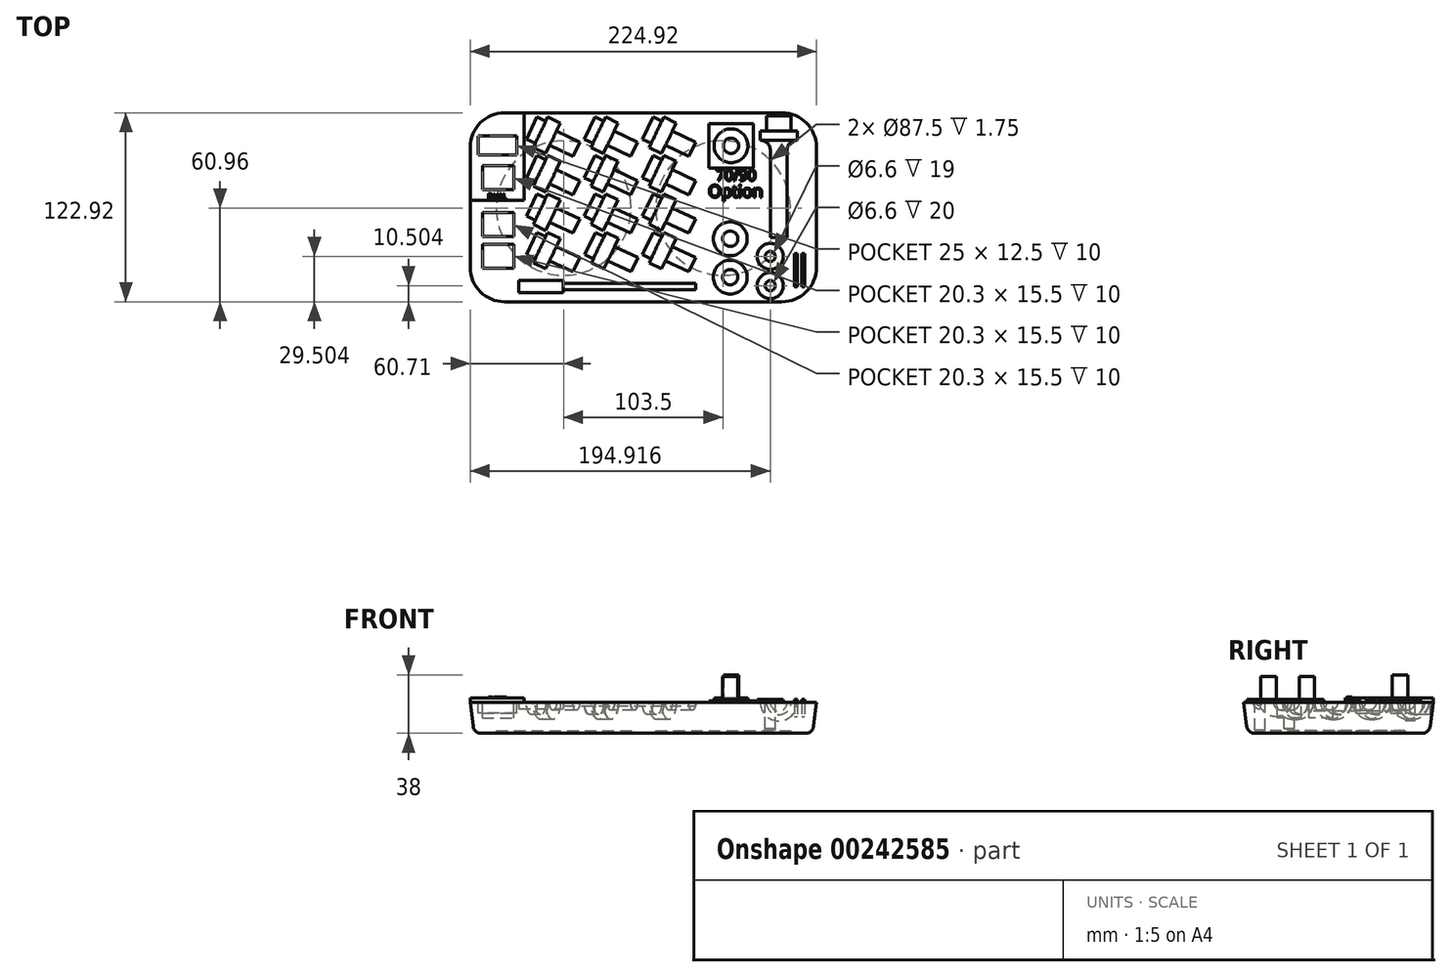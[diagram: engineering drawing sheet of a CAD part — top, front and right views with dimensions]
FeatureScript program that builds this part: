
annotation { "Feature Type Name" : "Feature", "Feature Type Description" : "" }
export const myFeature = defineFeature(function(context is Context, id is Id, definition is map)
    precondition{}
    {
        {
            var Q0;
            Q0=qCreatedBy(makeId("Top.planeOp"),FACE);
            var sketch = newSketch(context, id + "F0", { "sketchPlane" : qUnion([Q0])});
            skLineSegment(sketch, "E0.bottom", {"start": v(20, 0) * mm, "end": v(200, 0) * mm});
            skLineSegment(sketch, "E0.top", {"start": v(20, 118) * mm, "end": v(200, 118) * mm});
            skLineSegment(sketch, "E0.left", {"start": v(0, 20) * mm, "end": v(0, 98) * mm});
            skLineSegment(sketch, "E0.right", {"start": v(220, 20) * mm, "end": v(220, 98) * mm});
            skPoint(sketch, "E1.visualSharp", {"position": v(0, 118) * mm});
            skArc(sketch, "E1.filletArc", {"start": v(20, 118) * mm, "mid": v(5.86, 112.14) * mm, "end": v(0, 98) * mm});
            skPoint(sketch, "E2.visualSharp", {"position": v(220, 118) * mm});
            skArc(sketch, "E2.filletArc", {"start": v(220, 98) * mm, "mid": v(214.14, 112.14) * mm, "end": v(200, 118) * mm});
            skPoint(sketch, "E3.visualSharp", {"position": v(0, 0) * mm});
            skArc(sketch, "E3.filletArc", {"start": v(0, 20) * mm, "mid": v(5.86, 5.86) * mm, "end": v(20, 0) * mm});
            skPoint(sketch, "E4.visualSharp", {"position": v(220, 0) * mm});
            skArc(sketch, "E4.filletArc", {"start": v(200, 0) * mm, "mid": v(214.14, 5.86) * mm, "end": v(220, 20) * mm});
            skSolve(sketch);
        }
        {
            var Q0;
            Q0=makeQuery(id+"F0.imprint","IMPRINT",FACE,{"disambiguationData":[TD([[makeQuery(id+"F0.imprint","IMPRINT",EDGE,{"derivedFrom":sQuery(id+"F0.wireOp",EDGE,"E0.bottom")}),1.0]])]});
            extrude(context, id + "F1", {"entities" : qUnion([Q0]), "depth" : 20 * mm, "hasDraft" : true, "draftAngle" : 7 * degree});
        }
        {
            var Q0;
            Q0=makeQuery(id+"F1.opExtrude","CAP_FACE",FACE,{"disambiguationData":[OSD([sQuery(id+"F0.wireOp",EDGE,"E0.bottom"),sQuery(id+"F0.wireOp",EDGE,"E0.top"),sQuery(id+"F0.wireOp",EDGE,"E0.left"),sQuery(id+"F0.wireOp",EDGE,"E0.right"),sQuery(id+"F0.wireOp",EDGE,"E1.filletArc"),sQuery(id+"F0.wireOp",EDGE,"E2.filletArc"),sQuery(id+"F0.wireOp",EDGE,"E3.filletArc"),sQuery(id+"F0.wireOp",EDGE,"E4.filletArc")])],"isStart":true});
            fillet(context, id + "F2", {"entities" : qUnion([Q0]), "radius" : 5 * mm, "tangentPropagation" : true, "allowEdgeOverflow" : false});
        }
        {
            var Q0;
            Q0=makeQuery(id+"F1.opExtrude","CAP_FACE",FACE,{"disambiguationData":[OSD([sQuery(id+"F0.wireOp",EDGE,"E0.bottom"),sQuery(id+"F0.wireOp",EDGE,"E0.top"),sQuery(id+"F0.wireOp",EDGE,"E0.left"),sQuery(id+"F0.wireOp",EDGE,"E0.right"),sQuery(id+"F0.wireOp",EDGE,"E1.filletArc"),sQuery(id+"F0.wireOp",EDGE,"E2.filletArc"),sQuery(id+"F0.wireOp",EDGE,"E3.filletArc"),sQuery(id+"F0.wireOp",EDGE,"E4.filletArc")])],"isStart":true});
            var sketch = newSketch(context, id + "F3", { "sketchPlane" : qUnion([Q0])});
            skLineSegment(sketch, "E5.bottom", {"start": v(0, 0) * mm, "end": v(58.25, 0) * mm, "construction": true});
            skLineSegment(sketch, "E5.top", {"start": v(0, -58.5) * mm, "end": v(58.25, -58.5) * mm, "construction": true});
            skLineSegment(sketch, "E5.left", {"start": v(0, 0) * mm, "end": v(0, -58.5) * mm, "construction": true});
            skLineSegment(sketch, "E5.right", {"start": v(58.25, 0) * mm, "end": v(58.25, -58.5) * mm, "construction": true});
            skLineSegment(sketch, "E6.bottom", {"start": v(0, 0) * mm, "end": v(161.75, 0) * mm, "construction": true});
            skLineSegment(sketch, "E6.top", {"start": v(0, -58.5) * mm, "end": v(161.75, -58.5) * mm, "construction": true});
            skLineSegment(sketch, "E6.right", {"start": v(161.75, 0) * mm, "end": v(161.75, -58.5) * mm, "construction": true});
            skCircle(sketch, "E7", {"center": v(58.25, -58.5) * mm, "radius": 43.75 * mm});
            skCircle(sketch, "E8", {"center": v(161.75, -58.5) * mm, "radius": 43.75 * mm});
            skSolve(sketch);
        }
        {
            var Q0;
            Q0=qSketchRegion(id+"F3",true);
            extrude(context, id + "F4", {"entities" : qUnion([Q0]), "operationType" : NewBodyOperationType.REMOVE, "oppositeDirection" : true, "depth" : 1.75 * mm});
        }
        {
            var Q0;
            Q0=makeQuery(id+"F1.opExtrude","CAP_FACE",FACE,{"disambiguationData":[OSD([sQuery(id+"F0.wireOp",EDGE,"E0.bottom"),sQuery(id+"F0.wireOp",EDGE,"E0.top"),sQuery(id+"F0.wireOp",EDGE,"E0.left"),sQuery(id+"F0.wireOp",EDGE,"E0.right"),sQuery(id+"F0.wireOp",EDGE,"E1.filletArc"),sQuery(id+"F0.wireOp",EDGE,"E2.filletArc"),sQuery(id+"F0.wireOp",EDGE,"E3.filletArc"),sQuery(id+"F0.wireOp",EDGE,"E4.filletArc")])],"isStart":false});
            var sketch = newSketch(context, id + "F5", { "sketchPlane" : qUnion([Q0])});
            skLineSegment(sketch, "E9.bottom", {"start": v(-2.46, 63.45) * mm, "end": v(32.54, 63.45) * mm});
            skLineSegment(sketch, "E9.top", {"start": v(-2.46, 120.46) * mm, "end": v(32.54, 120.46) * mm});
            skLineSegment(sketch, "E9.left", {"start": v(-2.46, 63.45) * mm, "end": v(-2.46, 120.46) * mm});
            skLineSegment(sketch, "E9.right", {"start": v(32.54, 63.45) * mm, "end": v(32.54, 120.46) * mm});
            skSolve(sketch);
        }
        {
            var Q0;
            {var subQ1=sQuery(id+"F5.wireOp",EDGE,"E9.bottom");Q0=makeQuery(id+"F5.imprint","IMPRINT",FACE,{"disambiguationData":[TD([[makeQuery(id+"F5.imprint","IMPRINT",EDGE,{"derivedFrom":subQ1}),1.0]])]});}
            extrude(context, id + "F6", {"entities" : qUnion([Q0]), "operationType" : NewBodyOperationType.ADD, "depth" : 3 * mm});
        }
        {
            var Q0;
            Q0=makeQuery(id+"F6.opExtrude","CAP_FACE",FACE,{"disambiguationData":[OSD([sQuery(id+"F0.wireOp",EDGE,"E1.filletArc"),sQuery(id+"F5.wireOp",EDGE,"E9.bottom"),sQuery(id+"F5.wireOp",EDGE,"E9.top"),sQuery(id+"F5.wireOp",EDGE,"E9.left"),sQuery(id+"F5.wireOp",EDGE,"E9.right")])],"isStart":false});
            var sketch = newSketch(context, id + "F7", { "sketchPlane" : qUnion([Q0])});
            skText(sketch, "E10", { "text": "DUAL\n", "fontName": "OpenSans-Regular.ttf"});
            const initialGuessF7  = {"E10": [0.00892, 0.06446, 1, 0, 0.00342]};
            skSetInitialGuess(sketch, initialGuessF7);
            skSolve(sketch);
        }
        {
            var Q0;
            Q0 = qSketchRegion(id + "F7", true);
            extrude(context, id + "F8", {"entities" : qUnion([Q0]), "operationType" : NewBodyOperationType.ADD, "depth" : .5 * mm});
        }
        {
            var Q0;
            {var subQ0=sQuery(id+"F5.wireOp",EDGE,"E9.left");var subQ1=sQuery(id+"F5.wireOp",EDGE,"E9.top");var subQ2=sQuery(id+"F5.wireOp",EDGE,"E9.bottom");var subQ3=sQuery(id+"F5.wireOp",EDGE,"E9.right");var subQ4=sQuery(id+"F0.wireOp",EDGE,"E1.filletArc");Q0=makeQuery(id+"F8.boolean.opBoolean","SPLIT",FACE,{"disambiguationData":[TD([makeQuery(id+"F6.opExtrude","SWEPT_FACE",FACE,{"disambiguationData":[OSD([subQ2])]})])],"derivedFrom":makeQuery(id+"F6.opExtrude","CAP_FACE",FACE,{"disambiguationData":[OSD([subQ4,subQ2,subQ1,subQ0,subQ3])],"isStart":false})});}
            var sketch = newSketch(context, id + "F9", { "sketchPlane" : qUnion([Q0])});
            skSolve(sketch);
        }
        {
            var Q0;
            Q0=makeQuery(id+"F9.imprint","IMPRINT",FACE,{"disambiguationData":[TD([[makeQuery(id+"F9.imprint","IMPRINT",EDGE,{"derivedFrom":makeQuery(id+"F6.opExtrude","CAP_EDGE",EDGE,{"disambiguationData":[OSD([sQuery(id+"F5.wireOp",EDGE,"E9.bottom")])],"isStart":false})}),1.0]])]});
            var sketch = newSketch(context, id + "F10", { "sketchPlane" : qUnion([Q0])});
            skLineSegment(sketch, "E11.bottom", {"start": v(5.54, 70.45) * mm, "end": v(25.84, 70.45) * mm});
            skLineSegment(sketch, "E11.top", {"start": v(5.54, 85.95) * mm, "end": v(25.84, 85.95) * mm});
            skLineSegment(sketch, "E11.left", {"start": v(5.54, 70.45) * mm, "end": v(5.54, 85.95) * mm});
            skLineSegment(sketch, "E11.right", {"start": v(25.84, 70.45) * mm, "end": v(25.84, 85.95) * mm});
            skLineSegment(sketch, "E12.bottom", {"start": v(27.82, 92.95) * mm, "end": v(2.82, 92.95) * mm});
            skLineSegment(sketch, "E12.top", {"start": v(27.82, 105.45) * mm, "end": v(2.82, 105.45) * mm});
            skLineSegment(sketch, "E12.left", {"start": v(27.82, 92.95) * mm, "end": v(27.82, 105.45) * mm});
            skLineSegment(sketch, "E12.right", {"start": v(2.82, 92.95) * mm, "end": v(2.82, 105.45) * mm});
            skSolve(sketch);
        }
        {
            var Q0;
            Q0 = qSketchRegion(id + "F10", true);
            extrude(context, id + "F11", {"entities" : qUnion([Q0]), "operationType" : NewBodyOperationType.REMOVE, "oppositeDirection" : true, "depth" : 10 * mm});
        }
        {
            var Q0;
            Q0=makeQuery(id+"F1.opExtrude","CAP_FACE",FACE,{"disambiguationData":[OSD([sQuery(id+"F0.wireOp",EDGE,"E0.bottom"),sQuery(id+"F0.wireOp",EDGE,"E0.top"),sQuery(id+"F0.wireOp",EDGE,"E0.left"),sQuery(id+"F0.wireOp",EDGE,"E0.right"),sQuery(id+"F0.wireOp",EDGE,"E1.filletArc"),sQuery(id+"F0.wireOp",EDGE,"E2.filletArc"),sQuery(id+"F0.wireOp",EDGE,"E3.filletArc"),sQuery(id+"F0.wireOp",EDGE,"E4.filletArc")])],"isStart":false});
            var sketch = newSketch(context, id + "F12", { "sketchPlane" : qUnion([Q0])});
            skLineSegment(sketch, "E13.bottom", {"start": v(5.54, 55.45) * mm, "end": v(25.84, 55.45) * mm});
            skLineSegment(sketch, "E13.top", {"start": v(5.54, 39.95) * mm, "end": v(25.84, 39.95) * mm});
            skLineSegment(sketch, "E13.left", {"start": v(5.54, 55.45) * mm, "end": v(5.54, 39.95) * mm});
            skLineSegment(sketch, "E13.right", {"start": v(25.84, 55.45) * mm, "end": v(25.84, 39.95) * mm});
            skLineSegment(sketch, "E14.bottom", {"start": v(5.54, 34.95) * mm, "end": v(25.84, 34.95) * mm});
            skLineSegment(sketch, "E14.top", {"start": v(5.54, 19.45) * mm, "end": v(25.84, 19.45) * mm});
            skLineSegment(sketch, "E14.left", {"start": v(5.54, 34.95) * mm, "end": v(5.54, 19.45) * mm});
            skLineSegment(sketch, "E14.right", {"start": v(25.84, 34.95) * mm, "end": v(25.84, 19.45) * mm});
            skSolve(sketch);
        }
        {
            var Q0;
            Q0 = qSketchRegion(id + "F12", true);
            extrude(context, id + "F13", {"entities" : qUnion([Q0]), "operationType" : NewBodyOperationType.REMOVE, "oppositeDirection" : true, "depth" : 10 * mm});
        }
        {
            var Q0;
            Q0=makeQuery(id+"F1.opExtrude","CAP_FACE",FACE,{"disambiguationData":[OSD([sQuery(id+"F0.wireOp",EDGE,"E0.bottom"),sQuery(id+"F0.wireOp",EDGE,"E0.top"),sQuery(id+"F0.wireOp",EDGE,"E0.left"),sQuery(id+"F0.wireOp",EDGE,"E0.right"),sQuery(id+"F0.wireOp",EDGE,"E1.filletArc"),sQuery(id+"F0.wireOp",EDGE,"E2.filletArc"),sQuery(id+"F0.wireOp",EDGE,"E3.filletArc"),sQuery(id+"F0.wireOp",EDGE,"E4.filletArc")])],"isStart":false});
            var sketch = newSketch(context, id + "F14", { "sketchPlane" : qUnion([Q0])});
            skLineSegment(sketch, "E15", {"start": v(37.54, 110.46) * mm, "end": v(67.13, 96.37) * mm, "construction": true});
            skLineSegment(sketch, "E16", {"start": v(37.54, 110.46) * mm, "end": v(40.98, 117.68) * mm});
            skLineSegment(sketch, "E17", {"start": v(40.98, 117.68) * mm, "end": v(46.67, 114.97) * mm});
            skLineSegment(sketch, "E18", {"start": v(46.67, 114.97) * mm, "end": v(47.96, 117.68) * mm});
            skLineSegment(sketch, "E19", {"start": v(47.96, 117.68) * mm, "end": v(56.09, 113.8) * mm});
            skLineSegment(sketch, "E20", {"start": v(56.09, 113.8) * mm, "end": v(53.55, 108.48) * mm});
            skLineSegment(sketch, "E21", {"start": v(53.55, 108.48) * mm, "end": v(68.63, 101.3) * mm});
            skLineSegment(sketch, "E22", {"start": v(68.63, 101.3) * mm, "end": v(66.44, 96.7) * mm});
            skLineSegment(sketch, "E23", {"start": v(66.44, 96.7) * mm, "end": v(37.54, 110.46) * mm});
            skLineSegment(sketch, "E24.bottom", {"start": v(37.54, 110.46) * mm, "end": v(75.04, 110.46) * mm, "construction": true});
            skLineSegment(sketch, "E24.top", {"start": v(37.54, 85.46) * mm, "end": v(75.04, 85.46) * mm, "construction": true});
            skLineSegment(sketch, "E24.left", {"start": v(37.54, 110.46) * mm, "end": v(37.54, 85.46) * mm, "construction": true});
            skLineSegment(sketch, "E24.right", {"start": v(75.04, 110.46) * mm, "end": v(75.04, 85.46) * mm, "construction": true});
            skLineSegment(sketch, "E25", {"start": v(37.54, 85.46) * mm, "end": v(40.98, 92.68) * mm});
            skLineSegment(sketch, "E26", {"start": v(40.98, 92.68) * mm, "end": v(46.67, 89.97) * mm});
            skLineSegment(sketch, "E27", {"start": v(46.67, 89.97) * mm, "end": v(47.96, 92.68) * mm});
            skLineSegment(sketch, "E28", {"start": v(47.96, 92.68) * mm, "end": v(56.09, 88.8) * mm});
            skLineSegment(sketch, "E29", {"start": v(56.09, 88.8) * mm, "end": v(53.55, 83.48) * mm});
            skLineSegment(sketch, "E30", {"start": v(53.55, 83.48) * mm, "end": v(68.63, 76.3) * mm});
            skLineSegment(sketch, "E31", {"start": v(68.63, 76.3) * mm, "end": v(66.44, 71.7) * mm});
            skLineSegment(sketch, "E32", {"start": v(66.44, 71.7) * mm, "end": v(37.54, 85.46) * mm});
            skLineSegment(sketch, "E33.bottom", {"start": v(37.54, 85.46) * mm, "end": v(75.06, 85.46) * mm, "construction": true});
            skLineSegment(sketch, "E33.top", {"start": v(37.54, 60.46) * mm, "end": v(75.06, 60.46) * mm, "construction": true});
            skLineSegment(sketch, "E33.left", {"start": v(37.54, 85.46) * mm, "end": v(37.54, 60.46) * mm, "construction": true});
            skLineSegment(sketch, "E33.right", {"start": v(75.06, 85.46) * mm, "end": v(75.06, 60.46) * mm, "construction": true});
            skLineSegment(sketch, "E34.bottom", {"start": v(37.54, 60.46) * mm, "end": v(75.04, 60.46) * mm, "construction": true});
            skLineSegment(sketch, "E34.top", {"start": v(37.54, 35.46) * mm, "end": v(75.04, 35.46) * mm, "construction": true});
            skLineSegment(sketch, "E34.left", {"start": v(37.54, 60.46) * mm, "end": v(37.54, 35.46) * mm, "construction": true});
            skLineSegment(sketch, "E34.right", {"start": v(75.04, 60.46) * mm, "end": v(75.04, 35.46) * mm, "construction": true});
            skLineSegment(sketch, "E35.bottom", {"start": v(37.54, 35.46) * mm, "end": v(75.34, 35.46) * mm, "construction": true});
            skLineSegment(sketch, "E35.top", {"start": v(37.54, 10.46) * mm, "end": v(75.34, 10.46) * mm, "construction": true});
            skLineSegment(sketch, "E35.left", {"start": v(37.54, 35.46) * mm, "end": v(37.54, 10.46) * mm, "construction": true});
            skLineSegment(sketch, "E35.right", {"start": v(75.34, 35.46) * mm, "end": v(75.34, 10.46) * mm, "construction": true});
            skLineSegment(sketch, "E36.bottom", {"start": v(75.04, 110.46) * mm, "end": v(112.84, 110.46) * mm, "construction": true});
            skLineSegment(sketch, "E36.top", {"start": v(75.04, 85.46) * mm, "end": v(112.84, 85.46) * mm, "construction": true});
            skLineSegment(sketch, "E36.right", {"start": v(112.84, 110.46) * mm, "end": v(112.84, 85.46) * mm, "construction": true});
            skLineSegment(sketch, "E37.bottom", {"start": v(75.06, 85.46) * mm, "end": v(112.84, 85.46) * mm, "construction": true});
            skLineSegment(sketch, "E37.top", {"start": v(75.06, 60.46) * mm, "end": v(112.84, 60.46) * mm, "construction": true});
            skLineSegment(sketch, "E37.right", {"start": v(112.84, 85.46) * mm, "end": v(112.84, 60.46) * mm, "construction": true});
            skLineSegment(sketch, "E38.top", {"start": v(75.06, 35.46) * mm, "end": v(112.84, 35.46) * mm, "construction": true});
            skLineSegment(sketch, "E38.left", {"start": v(75.06, 60.46) * mm, "end": v(75.06, 35.46) * mm, "construction": true});
            skLineSegment(sketch, "E38.right", {"start": v(112.84, 60.46) * mm, "end": v(112.84, 35.46) * mm, "construction": true});
            skLineSegment(sketch, "E39.bottom", {"start": v(75.34, 35.46) * mm, "end": v(112.84, 35.46) * mm, "construction": true});
            skLineSegment(sketch, "E39.top", {"start": v(75.34, 10.46) * mm, "end": v(112.84, 10.46) * mm, "construction": true});
            skLineSegment(sketch, "E39.right", {"start": v(112.84, 35.46) * mm, "end": v(112.84, 10.46) * mm, "construction": true});
            skLineSegment(sketch, "E40.bottom", {"start": v(112.84, 110.46) * mm, "end": v(150.64, 110.46) * mm, "construction": true});
            skLineSegment(sketch, "E40.top", {"start": v(112.84, 85.46) * mm, "end": v(150.64, 85.46) * mm, "construction": true});
            skLineSegment(sketch, "E40.right", {"start": v(150.64, 110.46) * mm, "end": v(150.64, 85.46) * mm, "construction": true});
            skLineSegment(sketch, "E41.top", {"start": v(112.84, 60.46) * mm, "end": v(150.64, 60.46) * mm, "construction": true});
            skLineSegment(sketch, "E41.right", {"start": v(150.64, 85.46) * mm, "end": v(150.64, 60.46) * mm, "construction": true});
            skLineSegment(sketch, "E42.top", {"start": v(112.84, 35.46) * mm, "end": v(150.64, 35.46) * mm, "construction": true});
            skLineSegment(sketch, "E42.right", {"start": v(150.64, 60.46) * mm, "end": v(150.64, 35.46) * mm, "construction": true});
            skLineSegment(sketch, "E43.top", {"start": v(112.84, 10.46) * mm, "end": v(150.64, 10.46) * mm, "construction": true});
            skLineSegment(sketch, "E43.right", {"start": v(150.64, 35.46) * mm, "end": v(150.64, 10.46) * mm, "construction": true});
            skLineSegment(sketch, "E44", {"start": v(37.54, 60.46) * mm, "end": v(40.98, 67.68) * mm});
            skLineSegment(sketch, "E45", {"start": v(37.54, 35.46) * mm, "end": v(40.98, 42.68) * mm});
            skLineSegment(sketch, "E46", {"start": v(75.04, 110.46) * mm, "end": v(78.48, 117.68) * mm});
            skLineSegment(sketch, "E47", {"start": v(75.06, 85.46) * mm, "end": v(78.5, 92.68) * mm});
            skLineSegment(sketch, "E48", {"start": v(75.06, 60.46) * mm, "end": v(78.5, 67.68) * mm});
            skPoint(sketch, "E49.endSnap0", {"position": v(75.06, 47.96) * mm});
            skLineSegment(sketch, "E50", {"start": v(75.34, 35.46) * mm, "end": v(78.78, 42.68) * mm});
            skLineSegment(sketch, "E51", {"start": v(112.84, 35.46) * mm, "end": v(116.28, 42.68) * mm});
            skLineSegment(sketch, "E52", {"start": v(112.84, 60.46) * mm, "end": v(116.28, 67.68) * mm});
            skLineSegment(sketch, "E53", {"start": v(112.84, 85.46) * mm, "end": v(116.28, 92.68) * mm});
            skLineSegment(sketch, "E54", {"start": v(112.84, 110.46) * mm, "end": v(116.28, 117.68) * mm});
            skLineSegment(sketch, "E55", {"start": v(40.98, 67.68) * mm, "end": v(46.67, 64.97) * mm});
            skLineSegment(sketch, "E56", {"start": v(46.67, 64.97) * mm, "end": v(47.96, 67.68) * mm});
            skLineSegment(sketch, "E57", {"start": v(47.96, 67.68) * mm, "end": v(56.09, 63.8) * mm});
            skLineSegment(sketch, "E58", {"start": v(56.09, 63.8) * mm, "end": v(53.55, 58.48) * mm});
            skLineSegment(sketch, "E59", {"start": v(40.98, 42.68) * mm, "end": v(46.67, 39.97) * mm});
            skLineSegment(sketch, "E60", {"start": v(46.67, 39.97) * mm, "end": v(47.96, 42.68) * mm});
            skLineSegment(sketch, "E61", {"start": v(47.96, 42.68) * mm, "end": v(56.09, 38.8) * mm});
            skLineSegment(sketch, "E62", {"start": v(56.09, 38.8) * mm, "end": v(53.55, 33.48) * mm});
            skLineSegment(sketch, "E63", {"start": v(53.55, 33.48) * mm, "end": v(68.63, 26.3) * mm});
            skLineSegment(sketch, "E64", {"start": v(68.63, 26.3) * mm, "end": v(66.44, 21.7) * mm});
            skLineSegment(sketch, "E65", {"start": v(66.44, 21.7) * mm, "end": v(37.54, 35.46) * mm});
            skLineSegment(sketch, "E66", {"start": v(53.55, 58.48) * mm, "end": v(68.63, 51.3) * mm});
            skLineSegment(sketch, "E67", {"start": v(68.63, 51.3) * mm, "end": v(66.44, 46.7) * mm});
            skLineSegment(sketch, "E68", {"start": v(66.44, 46.7) * mm, "end": v(37.54, 60.46) * mm});
            skLineSegment(sketch, "E69", {"start": v(78.48, 117.68) * mm, "end": v(84.17, 114.97) * mm});
            skLineSegment(sketch, "E70", {"start": v(84.17, 114.97) * mm, "end": v(85.46, 117.68) * mm});
            skLineSegment(sketch, "E71", {"start": v(85.46, 117.68) * mm, "end": v(93.59, 113.8) * mm});
            skLineSegment(sketch, "E72", {"start": v(93.59, 113.8) * mm, "end": v(91.05, 108.48) * mm});
            skLineSegment(sketch, "E73", {"start": v(91.05, 108.48) * mm, "end": v(106.13, 101.3) * mm});
            skLineSegment(sketch, "E74", {"start": v(106.13, 101.3) * mm, "end": v(103.94, 96.7) * mm});
            skLineSegment(sketch, "E75", {"start": v(103.94, 96.7) * mm, "end": v(75.04, 110.46) * mm});
            skLineSegment(sketch, "E76", {"start": v(78.5, 92.68) * mm, "end": v(84.19, 89.97) * mm});
            skLineSegment(sketch, "E77", {"start": v(84.19, 89.97) * mm, "end": v(85.48, 92.68) * mm});
            skLineSegment(sketch, "E78", {"start": v(85.48, 92.68) * mm, "end": v(93.6, 88.8) * mm});
            skLineSegment(sketch, "E79", {"start": v(93.6, 88.8) * mm, "end": v(91.07, 83.48) * mm});
            skLineSegment(sketch, "E80", {"start": v(91.07, 83.48) * mm, "end": v(106.14, 76.3) * mm});
            skLineSegment(sketch, "E81", {"start": v(106.14, 76.3) * mm, "end": v(103.95, 71.7) * mm});
            skLineSegment(sketch, "E82", {"start": v(103.95, 71.7) * mm, "end": v(75.06, 85.46) * mm});
            skLineSegment(sketch, "E83", {"start": v(78.5, 67.68) * mm, "end": v(84.19, 64.97) * mm});
            skLineSegment(sketch, "E84", {"start": v(84.19, 64.97) * mm, "end": v(85.48, 67.68) * mm});
            skLineSegment(sketch, "E85", {"start": v(85.48, 67.68) * mm, "end": v(93.6, 63.8) * mm});
            skLineSegment(sketch, "E86", {"start": v(93.6, 63.8) * mm, "end": v(91.07, 58.48) * mm});
            skLineSegment(sketch, "E87", {"start": v(91.07, 58.48) * mm, "end": v(106.14, 51.3) * mm});
            skLineSegment(sketch, "E88", {"start": v(106.14, 51.3) * mm, "end": v(103.95, 46.7) * mm});
            skLineSegment(sketch, "E89", {"start": v(103.95, 46.7) * mm, "end": v(75.06, 60.46) * mm});
            skLineSegment(sketch, "E90", {"start": v(78.78, 42.68) * mm, "end": v(84.47, 39.97) * mm});
            skLineSegment(sketch, "E91", {"start": v(84.47, 39.97) * mm, "end": v(85.76, 42.68) * mm});
            skLineSegment(sketch, "E92", {"start": v(85.76, 42.68) * mm, "end": v(93.88, 38.8) * mm});
            skLineSegment(sketch, "E93", {"start": v(93.88, 38.8) * mm, "end": v(91.35, 33.48) * mm});
            skLineSegment(sketch, "E94", {"start": v(91.35, 33.48) * mm, "end": v(106.42, 26.3) * mm});
            skLineSegment(sketch, "E95", {"start": v(106.42, 26.3) * mm, "end": v(104.23, 21.7) * mm});
            skLineSegment(sketch, "E96", {"start": v(104.23, 21.7) * mm, "end": v(75.34, 35.46) * mm});
            skLineSegment(sketch, "E97", {"start": v(116.28, 117.68) * mm, "end": v(121.97, 114.97) * mm});
            skLineSegment(sketch, "E98", {"start": v(121.97, 114.97) * mm, "end": v(123.26, 117.68) * mm});
            skLineSegment(sketch, "E99", {"start": v(123.26, 117.68) * mm, "end": v(131.38, 113.8) * mm});
            skLineSegment(sketch, "E100", {"start": v(131.38, 113.8) * mm, "end": v(128.85, 108.48) * mm});
            skLineSegment(sketch, "E101", {"start": v(128.85, 108.48) * mm, "end": v(143.92, 101.3) * mm});
            skLineSegment(sketch, "E102", {"start": v(143.92, 101.3) * mm, "end": v(141.73, 96.7) * mm});
            skLineSegment(sketch, "E103", {"start": v(141.73, 96.7) * mm, "end": v(112.84, 110.46) * mm});
            skLineSegment(sketch, "E104", {"start": v(116.28, 92.68) * mm, "end": v(121.97, 89.97) * mm});
            skLineSegment(sketch, "E105", {"start": v(121.97, 89.97) * mm, "end": v(123.26, 92.68) * mm});
            skLineSegment(sketch, "E106", {"start": v(123.26, 92.68) * mm, "end": v(131.38, 88.8) * mm});
            skLineSegment(sketch, "E107", {"start": v(131.38, 88.8) * mm, "end": v(128.85, 83.48) * mm});
            skLineSegment(sketch, "E108", {"start": v(128.85, 83.48) * mm, "end": v(143.92, 76.3) * mm});
            skLineSegment(sketch, "E109", {"start": v(143.92, 76.3) * mm, "end": v(141.73, 71.7) * mm});
            skLineSegment(sketch, "E110", {"start": v(141.73, 71.7) * mm, "end": v(112.84, 85.46) * mm});
            skLineSegment(sketch, "E111", {"start": v(116.28, 67.68) * mm, "end": v(121.97, 64.97) * mm});
            skLineSegment(sketch, "E112", {"start": v(121.97, 64.97) * mm, "end": v(123.26, 67.68) * mm});
            skLineSegment(sketch, "E113", {"start": v(123.26, 67.68) * mm, "end": v(131.38, 63.8) * mm});
            skLineSegment(sketch, "E114", {"start": v(131.38, 63.8) * mm, "end": v(128.85, 58.48) * mm});
            skLineSegment(sketch, "E115", {"start": v(128.85, 58.48) * mm, "end": v(143.92, 51.3) * mm});
            skLineSegment(sketch, "E116", {"start": v(143.92, 51.3) * mm, "end": v(141.73, 46.7) * mm});
            skLineSegment(sketch, "E117", {"start": v(141.73, 46.7) * mm, "end": v(112.84, 60.46) * mm});
            skLineSegment(sketch, "E118", {"start": v(116.28, 42.68) * mm, "end": v(121.97, 39.97) * mm});
            skLineSegment(sketch, "E119", {"start": v(121.97, 39.97) * mm, "end": v(123.26, 42.68) * mm});
            skLineSegment(sketch, "E120", {"start": v(123.26, 42.68) * mm, "end": v(131.38, 38.8) * mm});
            skLineSegment(sketch, "E121", {"start": v(131.38, 38.8) * mm, "end": v(128.85, 33.48) * mm});
            skLineSegment(sketch, "E122", {"start": v(128.85, 33.48) * mm, "end": v(143.92, 26.3) * mm});
            skLineSegment(sketch, "E123", {"start": v(143.92, 26.3) * mm, "end": v(141.73, 21.7) * mm});
            skLineSegment(sketch, "E124", {"start": v(141.73, 21.7) * mm, "end": v(112.84, 35.46) * mm});
            skSolve(sketch);
        }
        {
            var Q0;
            Q0=makeQuery(id+"F14.imprint","IMPRINT",FACE,{"disambiguationData":[TD([[makeQuery(id+"F14.imprint","IMPRINT",EDGE,{"derivedFrom":sQuery(id+"F14.wireOp",EDGE,"E16")}),-1.0]])]});
            var Q1;
            Q1=sQuery(id+"F14.wireOp",EDGE,"E23");
            revolve(context, id + "F15", {"operationType" : NewBodyOperationType.REMOVE, "entities" : qUnion([Q0]), "axis" : qUnion([Q1]), "revolveType" : RevolveType.FULL, "oppositeDirection" : true});
        }
        {
            var Q0;
            Q0=makeQuery(id+"F14.imprint","IMPRINT",FACE,{"disambiguationData":[TD([[makeQuery(id+"F14.imprint","IMPRINT",EDGE,{"derivedFrom":sQuery(id+"F14.wireOp",EDGE,"E25")}),-1.0]])]});
            var Q1;
            Q1=sQuery(id+"F14.wireOp",EDGE,"E32");
            revolve(context, id + "F16", {"operationType" : NewBodyOperationType.REMOVE, "entities" : qUnion([Q0]), "axis" : qUnion([Q1]), "revolveType" : RevolveType.FULL, "oppositeDirection" : true});
        }
        {
            var Q0;
            Q0=makeQuery(id+"F14.imprint","IMPRINT",FACE,{"disambiguationData":[TD([[makeQuery(id+"F14.imprint","IMPRINT",EDGE,{"derivedFrom":sQuery(id+"F14.wireOp",EDGE,"E44")}),-1.0]])]});
            var Q1;
            Q1=sQuery(id+"F14.wireOp",EDGE,"E68");
            revolve(context, id + "F17", {"operationType" : NewBodyOperationType.REMOVE, "entities" : qUnion([Q0]), "axis" : qUnion([Q1]), "revolveType" : RevolveType.FULL, "oppositeDirection" : true});
        }
        {
            var Q0;
            Q0=makeQuery(id+"F14.imprint","IMPRINT",FACE,{"disambiguationData":[TD([[makeQuery(id+"F14.imprint","IMPRINT",EDGE,{"derivedFrom":sQuery(id+"F14.wireOp",EDGE,"E45")}),-1.0]])]});
            var Q1;
            Q1=sQuery(id+"F14.wireOp",EDGE,"E65");
            revolve(context, id + "F18", {"operationType" : NewBodyOperationType.REMOVE, "entities" : qUnion([Q0]), "axis" : qUnion([Q1]), "revolveType" : RevolveType.FULL, "oppositeDirection" : true});
        }
        {
            var Q0;
            Q0=makeQuery(id+"F14.imprint","IMPRINT",FACE,{"disambiguationData":[TD([[makeQuery(id+"F14.imprint","IMPRINT",EDGE,{"derivedFrom":sQuery(id+"F14.wireOp",EDGE,"E46")}),-1.0]])]});
            var Q1;
            Q1=sQuery(id+"F14.wireOp",EDGE,"E75");
            revolve(context, id + "F19", {"operationType" : NewBodyOperationType.REMOVE, "entities" : qUnion([Q0]), "axis" : qUnion([Q1]), "revolveType" : RevolveType.FULL, "oppositeDirection" : true});
        }
        {
            var Q0;
            Q0=makeQuery(id+"F14.imprint","IMPRINT",FACE,{"disambiguationData":[TD([[makeQuery(id+"F14.imprint","IMPRINT",EDGE,{"derivedFrom":sQuery(id+"F14.wireOp",EDGE,"E47")}),-1.0]])]});
            var Q1;
            Q1=sQuery(id+"F14.wireOp",EDGE,"E82");
            revolve(context, id + "F20", {"operationType" : NewBodyOperationType.REMOVE, "entities" : qUnion([Q0]), "axis" : qUnion([Q1]), "revolveType" : RevolveType.FULL, "oppositeDirection" : true});
        }
        {
            var Q0;
            Q0=makeQuery(id+"F14.imprint","IMPRINT",FACE,{"disambiguationData":[TD([[makeQuery(id+"F14.imprint","IMPRINT",EDGE,{"derivedFrom":sQuery(id+"F14.wireOp",EDGE,"E54")}),-1.0]])]});
            var Q1;
            Q1=sQuery(id+"F14.wireOp",EDGE,"E103");
            revolve(context, id + "F21", {"operationType" : NewBodyOperationType.REMOVE, "entities" : qUnion([Q0]), "axis" : qUnion([Q1]), "revolveType" : RevolveType.FULL, "oppositeDirection" : true});
        }
        {
            var Q0;
            Q0=makeQuery(id+"F14.imprint","IMPRINT",FACE,{"disambiguationData":[TD([[makeQuery(id+"F14.imprint","IMPRINT",EDGE,{"derivedFrom":sQuery(id+"F14.wireOp",EDGE,"E51")}),-1.0]])]});
            var Q1;
            Q1=sQuery(id+"F14.wireOp",EDGE,"E124");
            revolve(context, id + "F22", {"operationType" : NewBodyOperationType.REMOVE, "entities" : qUnion([Q0]), "axis" : qUnion([Q1]), "revolveType" : RevolveType.FULL, "oppositeDirection" : true});
        }
        {
            var Q0;
            Q0=makeQuery(id+"F14.imprint","IMPRINT",FACE,{"disambiguationData":[TD([[makeQuery(id+"F14.imprint","IMPRINT",EDGE,{"derivedFrom":sQuery(id+"F14.wireOp",EDGE,"E53")}),-1.0]])]});
            var Q1;
            Q1=sQuery(id+"F14.wireOp",EDGE,"E110");
            revolve(context, id + "F23", {"operationType" : NewBodyOperationType.REMOVE, "entities" : qUnion([Q0]), "axis" : qUnion([Q1]), "revolveType" : RevolveType.FULL, "oppositeDirection" : true});
        }
        {
            var Q0;
            Q0=makeQuery(id+"F14.imprint","IMPRINT",FACE,{"disambiguationData":[TD([[makeQuery(id+"F14.imprint","IMPRINT",EDGE,{"derivedFrom":sQuery(id+"F14.wireOp",EDGE,"E52")}),-1.0]])]});
            var Q1;
            Q1=sQuery(id+"F14.wireOp",EDGE,"E117");
            revolve(context, id + "F24", {"operationType" : NewBodyOperationType.REMOVE, "entities" : qUnion([Q0]), "axis" : qUnion([Q1]), "revolveType" : RevolveType.FULL, "oppositeDirection" : true});
        }
        {
            var Q0;
            Q0=makeQuery(id+"F14.imprint","IMPRINT",FACE,{"disambiguationData":[TD([[makeQuery(id+"F14.imprint","IMPRINT",EDGE,{"derivedFrom":sQuery(id+"F14.wireOp",EDGE,"E48")}),-1.0]])]});
            var Q1;
            Q1=sQuery(id+"F14.wireOp",EDGE,"E89");
            revolve(context, id + "F25", {"operationType" : NewBodyOperationType.REMOVE, "entities" : qUnion([Q0]), "axis" : qUnion([Q1]), "revolveType" : RevolveType.FULL, "oppositeDirection" : true});
        }
        {
            var Q0;
            Q0=makeQuery(id+"F14.imprint","IMPRINT",FACE,{"disambiguationData":[TD([[makeQuery(id+"F14.imprint","IMPRINT",EDGE,{"derivedFrom":sQuery(id+"F14.wireOp",EDGE,"E50")}),-1.0]])]});
            var Q1;
            Q1=sQuery(id+"F14.wireOp",EDGE,"E96");
            revolve(context, id + "F26", {"operationType" : NewBodyOperationType.REMOVE, "entities" : qUnion([Q0]), "axis" : qUnion([Q1]), "revolveType" : RevolveType.FULL, "oppositeDirection" : true});
        }
        {
            var Q0;
            Q0=makeQuery(id+"F14.imprint","IMPRINT",FACE,{"disambiguationData":[TD([[makeQuery(id+"F14.imprint","IMPRINT",EDGE,{"derivedFrom":sQuery(id+"F14.wireOp",EDGE,"E16")}),1.0]])]});
            var sketch = newSketch(context, id + "F27", { "sketchPlane" : qUnion([Q0])});
            skLineSegment(sketch, "E125.bottom", {"start": v(152.46, 113.46) * mm, "end": v(181.46, 113.46) * mm});
            skLineSegment(sketch, "E125.top", {"start": v(152.46, 84.46) * mm, "end": v(181.46, 84.46) * mm});
            skLineSegment(sketch, "E125.left", {"start": v(152.46, 113.46) * mm, "end": v(152.46, 84.46) * mm});
            skLineSegment(sketch, "E125.right", {"start": v(181.46, 113.46) * mm, "end": v(181.46, 84.46) * mm});
            skLineSegment(sketch, "E126", {"start": v(152.46, 84.46) * mm, "end": v(181.46, 113.46) * mm, "construction": true});
            skLineSegment(sketch, "E127", {"start": v(152.46, 113.46) * mm, "end": v(181.46, 84.46) * mm, "construction": true});
            skSolve(sketch);
        }
        {
            var Q0;
            Q0 = qSketchRegion(id + "F27", true);
            extrude(context, id + "F28", {"entities" : qUnion([Q0]), "operationType" : NewBodyOperationType.ADD, "depth" : 1 * mm});
        }
        {
            var Q0;
            Q0=makeQuery(id+"F28.opExtrude","CAP_FACE",FACE,{"disambiguationData":[OSD([sQuery(id+"F27.wireOp",EDGE,"E125.bottom"),sQuery(id+"F27.wireOp",EDGE,"E125.top"),sQuery(id+"F27.wireOp",EDGE,"E125.left"),sQuery(id+"F27.wireOp",EDGE,"E125.right")])],"isStart":false});
            var sketch = newSketch(context, id + "F29", { "sketchPlane" : qUnion([Q0])});
            skLineSegment(sketch, "E128", {"start": v(152.46, 84.46) * mm, "end": v(181.46, 113.46) * mm, "construction": true});
            skLineSegment(sketch, "E129", {"start": v(181.46, 113.46) * mm, "end": v(152.46, 113.46) * mm, "construction": true});
            skLineSegment(sketch, "E130", {"start": v(152.46, 113.46) * mm, "end": v(181.46, 84.46) * mm, "construction": true});
            skCircle(sketch, "E131", {"center": v(166.96, 98.96) * mm, "radius": 11 * mm});
            skSolve(sketch);
        }
        {
            var Q0;
            Q0 = qSketchRegion(id + "F29", true);
            extrude(context, id + "F30", {"entities" : qUnion([Q0]), "operationType" : NewBodyOperationType.ADD, "depth" : 2 * mm});
        }
        {
            var Q0;
            Q0=makeQuery(id+"F30.opExtrude","CAP_FACE",FACE,{"disambiguationData":[OSD([sQuery(id+"F29.wireOp",EDGE,"E131")])],"isStart":false});
            var sketch = newSketch(context, id + "F31", { "sketchPlane" : qUnion([Q0])});
            skCircle(sketch, "E132", {"center": v(166.96, 98.96) * mm, "radius": 5 * mm});
            skSolve(sketch);
        }
        {
            var Q0;
            Q0 = qSketchRegion(id + "F31", true);
            extrude(context, id + "F32", {"entities" : qUnion([Q0]), "operationType" : NewBodyOperationType.ADD, "depth" : 15 * mm});
        }
        {
            var Q0;
            Q0=makeQuery(id+"F14.imprint","IMPRINT",FACE,{"disambiguationData":[TD([[makeQuery(id+"F14.imprint","IMPRINT",EDGE,{"derivedFrom":sQuery(id+"F14.wireOp",EDGE,"E16")}),1.0]])]});
            var sketch = newSketch(context, id + "F33", { "sketchPlane" : qUnion([Q0])});
            skCircle(sketch, "E133", {"center": v(166.46, 38.54) * mm, "radius": 11 * mm});
            skCircle(sketch, "E134", {"center": v(166.46, 13.54) * mm, "radius": 11 * mm});
            skSolve(sketch);
        }
        {
            var Q0;
            Q0 = qSketchRegion(id + "F33", true);
            extrude(context, id + "F34", {"entities" : qUnion([Q0]), "operationType" : NewBodyOperationType.ADD, "depth" : 2 * mm});
        }
        {
            var Q0;
            Q0=makeQuery(id+"F34.opExtrude","CAP_FACE",FACE,{"disambiguationData":[OSD([sQuery(id+"F33.wireOp",EDGE,"E133")])],"isStart":false});
            var sketch = newSketch(context, id + "F35", { "sketchPlane" : qUnion([Q0])});
            skCircle(sketch, "E135", {"center": v(166.46, 38.54) * mm, "radius": 5 * mm});
            skSolve(sketch);
        }
        {
            var Q0;
            Q0=makeQuery(id+"F34.opExtrude","CAP_FACE",FACE,{"disambiguationData":[OSD([sQuery(id+"F33.wireOp",EDGE,"E134")])],"isStart":false});
            var sketch = newSketch(context, id + "F36", { "sketchPlane" : qUnion([Q0])});
            skCircle(sketch, "E136", {"center": v(166.46, 13.54) * mm, "radius": 5 * mm});
            skSolve(sketch);
        }
        {
            var Q0;
            Q0 = qSketchRegion(id + "F36", true);
            extrude(context, id + "F37", {"entities" : qUnion([Q0]), "operationType" : NewBodyOperationType.ADD, "depth" : 15 * mm});
        }
        {
            var Q0;
            Q0 = qSketchRegion(id + "F35", true);
            extrude(context, id + "F38", {"entities" : qUnion([Q0]), "operationType" : NewBodyOperationType.ADD, "depth" : 15 * mm});
        }
        {
            var Q0;
            Q0=makeQuery(id+"F14.imprint","IMPRINT",FACE,{"disambiguationData":[TD([[makeQuery(id+"F14.imprint","IMPRINT",EDGE,{"derivedFrom":sQuery(id+"F14.wireOp",EDGE,"E16")}),1.0]])]});
            var sketch = newSketch(context, id + "F39", { "sketchPlane" : qUnion([Q0])});
            skText(sketch, "E137", { "text": "70/90", "fontName": "OpenSans-Regular.ttf"});
            const initialGuessF39  = {"E137": [0.1571, 0.07634, 1, 0, 0.00711]};
            skSetInitialGuess(sketch, initialGuessF39);
            skSolve(sketch);
        }
        {
            var Q0;
            Q0 = qSketchRegion(id + "F39", true);
            extrude(context, id + "F40", {"entities" : qUnion([Q0]), "operationType" : NewBodyOperationType.ADD, "depth" : 1 * mm});
        }
        {
            var Q0;
            Q0=makeQuery(id+"F14.imprint","IMPRINT",FACE,{"disambiguationData":[TD([[makeQuery(id+"F14.imprint","IMPRINT",EDGE,{"derivedFrom":sQuery(id+"F14.wireOp",EDGE,"E16")}),1.0]])]});
            var sketch = newSketch(context, id + "F41", { "sketchPlane" : qUnion([Q0])});
            skText(sketch, "E138", { "text": "Option", "fontName": "OpenSans-Regular.ttf"});
            const initialGuessF41  = {"E138": [0.15217, 0.06552, 1, 0, 0.00794]};
            skSetInitialGuess(sketch, initialGuessF41);
            skSolve(sketch);
        }
        {
            var Q0;
            Q0 = qSketchRegion(id + "F41", true);
            extrude(context, id + "F42", {"entities" : qUnion([Q0]), "operationType" : NewBodyOperationType.ADD, "depth" : 1 * mm});
        }
        {
            var Q0;
            Q0=makeQuery(id+"F14.imprint","IMPRINT",FACE,{"disambiguationData":[TD([[makeQuery(id+"F14.imprint","IMPRINT",EDGE,{"derivedFrom":sQuery(id+"F14.wireOp",EDGE,"E16")}),1.0]])]});
            var sketch = newSketch(context, id + "F43", { "sketchPlane" : qUnion([Q0])});
            skCircle(sketch, "E139", {"center": v(192.46, 8.04) * mm, "radius": 8.5 * mm});
            skLineSegment(sketch, "E140", {"start": v(192.46, 8.04) * mm, "end": v(192.46, 128.14) * mm, "construction": true});
            skCircle(sketch, "E141", {"center": v(192.46, 27.04) * mm, "radius": 8.5 * mm});
            skLineSegment(sketch, "E142.bottom", {"start": v(208.08, 7.15) * mm, "end": v(210.08, 7.15) * mm});
            skLineSegment(sketch, "E142.top", {"start": v(208.08, 18.15) * mm, "end": v(210.08, 18.15) * mm});
            skLineSegment(sketch, "E142.left", {"start": v(208.08, 7.15) * mm, "end": v(208.08, 18.15) * mm});
            skLineSegment(sketch, "E142.right", {"start": v(210.08, 7.15) * mm, "end": v(210.08, 18.15) * mm});
            skLineSegment(sketch, "E143.bottom", {"start": v(212.82, 7.15) * mm, "end": v(214.82, 7.15) * mm});
            skLineSegment(sketch, "E143.top", {"start": v(212.82, 18.15) * mm, "end": v(214.82, 18.15) * mm});
            skLineSegment(sketch, "E143.left", {"start": v(212.82, 7.15) * mm, "end": v(212.82, 18.15) * mm});
            skLineSegment(sketch, "E143.right", {"start": v(214.82, 7.15) * mm, "end": v(214.82, 18.15) * mm});
            skSolve(sketch);
        }
        {
            var Q0;
            Q0 = qSketchRegion(id + "F43", true);
            extrude(context, id + "F44", {"entities" : qUnion([Q0]), "operationType" : NewBodyOperationType.ADD, "depth" : 2 * mm});
        }
        {
            var Q0;
            Q0=makeQuery(id+"F44.opExtrude","CAP_FACE",FACE,{"disambiguationData":[OSD([sQuery(id+"F43.wireOp",EDGE,"E141")])],"isStart":false});
            var sketch = newSketch(context, id + "F45", { "sketchPlane" : qUnion([Q0])});
            skCircle(sketch, "E144", {"center": v(192.46, 27.04) * mm, "radius": 3.3 * mm});
            skSolve(sketch);
        }
        {
            var Q0;
            Q0 = qSketchRegion(id + "F45", true);
            extrude(context, id + "F46", {"entities" : qUnion([Q0]), "operationType" : NewBodyOperationType.REMOVE, "oppositeDirection" : true, "depth" : 19 * mm});
        }
        {
            var Q0;
            Q0=makeQuery(id+"F44.opExtrude","CAP_FACE",FACE,{"disambiguationData":[OSD([sQuery(id+"F43.wireOp",EDGE,"E139")])],"isStart":false});
            var sketch = newSketch(context, id + "F47", { "sketchPlane" : qUnion([Q0])});
            skCircle(sketch, "E145", {"center": v(192.46, 8.04) * mm, "radius": 3.3 * mm});
            skSolve(sketch);
        }
        {
            var Q0;
            Q0 = qSketchRegion(id + "F47", true);
            extrude(context, id + "F48", {"entities" : qUnion([Q0]), "operationType" : NewBodyOperationType.REMOVE, "oppositeDirection" : true, "depth" : 20 * mm});
        }
        {
            var Q0;
            Q0=makeQuery(id+"F14.imprint","IMPRINT",FACE,{"disambiguationData":[TD([[makeQuery(id+"F14.imprint","IMPRINT",EDGE,{"derivedFrom":sQuery(id+"F14.wireOp",EDGE,"E16")}),1.0]])]});
            var sketch = newSketch(context, id + "F49", { "sketchPlane" : qUnion([Q0])});
            skLineSegment(sketch, "E146.bottom", {"start": v(29.08, 3.54) * mm, "end": v(58.08, 3.54) * mm});
            skLineSegment(sketch, "E146.top", {"start": v(29.08, 7.54) * mm, "end": v(58.08, 7.54) * mm});
            skLineSegment(sketch, "E146.left", {"start": v(29.08, 3.54) * mm, "end": v(29.08, 7.54) * mm});
            skLineSegment(sketch, "E146.right", {"start": v(58.08, 3.54) * mm, "end": v(58.08, 7.54) * mm});
            skLineSegment(sketch, "E147.bottom", {"start": v(58.08, 7.54) * mm, "end": v(144.08, 7.54) * mm});
            skLineSegment(sketch, "E147.top", {"start": v(58.08, 5.54) * mm, "end": v(144.08, 5.54) * mm});
            skLineSegment(sketch, "E147.left", {"start": v(58.08, 7.54) * mm, "end": v(58.08, 5.54) * mm});
            skLineSegment(sketch, "E147.right", {"start": v(144.08, 7.54) * mm, "end": v(144.08, 5.54) * mm});
            skSolve(sketch);
        }
        {
            var Q0;
            Q0 = qSketchRegion(id + "F49", true);
            var Q1;
            Q1=sQuery(id+"F49.wireOp",EDGE,"E146.top");
            revolve(context, id + "F50", {"operationType" : NewBodyOperationType.REMOVE, "entities" : qUnion([Q0]), "axis" : qUnion([Q1]), "revolveType" : RevolveType.FULL, "oppositeDirection" : true});
        }
        {
            var Q0;
            Q0=makeQuery(id+"F44.opExtrude","CAP_FACE",FACE,{"disambiguationData":[OSD([sQuery(id+"F43.wireOp",EDGE,"E142.bottom"),sQuery(id+"F43.wireOp",EDGE,"E142.top"),sQuery(id+"F43.wireOp",EDGE,"E142.left"),sQuery(id+"F43.wireOp",EDGE,"E142.right")])],"isStart":false});
            var Q1;
            Q1=makeQuery(id+"F44.opExtrude","CAP_FACE",FACE,{"disambiguationData":[OSD([sQuery(id+"F43.wireOp",EDGE,"E143.bottom"),sQuery(id+"F43.wireOp",EDGE,"E143.top"),sQuery(id+"F43.wireOp",EDGE,"E143.left"),sQuery(id+"F43.wireOp",EDGE,"E143.right")])],"isStart":false});
            var Q2;
            Q2=makeQuery(id+"F44.opExtrude","CAP_EDGE",EDGE,{"disambiguationData":[OSD([sQuery(id+"F43.wireOp",EDGE,"E143.top")])],"isStart":false});
            revolve(context, id + "F51", {"operationType" : NewBodyOperationType.REMOVE, "entities" : qUnion([Q0, Q1]), "axis" : qUnion([Q2]), "revolveType" : RevolveType.FULL, "oppositeDirection" : true});
        }
        {
            var Q0;
            Q0=makeQuery(id+"F14.imprint","IMPRINT",FACE,{"disambiguationData":[TD([[makeQuery(id+"F14.imprint","IMPRINT",EDGE,{"derivedFrom":sQuery(id+"F14.wireOp",EDGE,"E16")}),1.0]])]});
            var sketch = newSketch(context, id + "F52", { "sketchPlane" : qUnion([Q0])});
            skLineSegment(sketch, "E148.bottom", {"start": v(197.96, 118.46) * mm, "end": v(205.96, 118.46) * mm});
            skLineSegment(sketch, "E148.top", {"start": v(197.96, 108.46) * mm, "end": v(205.96, 108.46) * mm});
            skLineSegment(sketch, "E148.left", {"start": v(197.96, 118.46) * mm, "end": v(197.96, 108.46) * mm});
            skLineSegment(sketch, "E148.right", {"start": v(205.96, 118.46) * mm, "end": v(205.96, 108.46) * mm});
            skLineSegment(sketch, "E149.bottom", {"start": v(197.96, 108.46) * mm, "end": v(209.96, 108.46) * mm});
            skLineSegment(sketch, "E149.top", {"start": v(197.96, 102.46) * mm, "end": v(209.96, 102.46) * mm});
            skLineSegment(sketch, "E149.left", {"start": v(197.96, 108.46) * mm, "end": v(197.96, 102.46) * mm});
            skLineSegment(sketch, "E149.right", {"start": v(209.96, 108.46) * mm, "end": v(209.96, 102.46) * mm});
            skLineSegment(sketch, "E150.bottom", {"start": v(197.96, 102.46) * mm, "end": v(203.46, 102.46) * mm});
            skLineSegment(sketch, "E150.top", {"start": v(197.96, 39.46) * mm, "end": v(203.46, 39.46) * mm});
            skLineSegment(sketch, "E150.left", {"start": v(197.96, 102.46) * mm, "end": v(197.96, 39.46) * mm});
            skLineSegment(sketch, "E150.right", {"start": v(203.46, 102.46) * mm, "end": v(203.46, 39.46) * mm});
            skSolve(sketch);
        }
        {
            var Q0;
            Q0 = qSketchRegion(id + "F52", true);
            var Q1;
            Q1=sQuery(id+"F52.wireOp",EDGE,"E150.left");
            revolve(context, id + "F53", {"operationType" : NewBodyOperationType.REMOVE, "entities" : qUnion([Q0]), "axis" : qUnion([Q1]), "revolveType" : RevolveType.FULL, "oppositeDirection" : true});
        }
        {
            var Q0;
            Q0=makeQuery(id+"F53.boolean.opBoolean","COPY",EDGE,{"derivedFrom":makeQuery(id+"F53.opRevolve","SWEPT_EDGE",EDGE,{"disambiguationData":[OSD([sQuery(id+"F52.wireOp",EDGE,"E149.top"),sQuery(id+"F52.wireOp",EDGE,"E150.bottom"),sQuery(id+"F52.wireOp",EDGE,"E150.right")])]})});
            fillet(context, id + "F54", {"entities" : qUnion([Q0]), "radius" : 6 * mm, "tangentPropagation" : true, "allowEdgeOverflow" : false});
        }
    });
